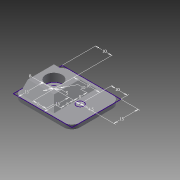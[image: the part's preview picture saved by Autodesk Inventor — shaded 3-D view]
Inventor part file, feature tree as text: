
AUTODESK INVENTOR PART (.ipt)
format: ipt  version: 2015 (Build 190159000, 159)  size: 124,416 bytes
history: native  units: mm
features: fillet x4, extrude x3, chamfer x3, sketch x1
ambient origin geometry x8: Origin, YZ Plane, XZ Plane, XY Plane, X Axis, Y Axis, Z Axis, Center Point
bodies: Solid1 (feature_tree)
feature tree (11):
  sketch  "Sketch1"  dims[d0=10.0mm d1=16.0mm d2=4.5mm d3=5.0mm d4=15.0mm d5=15.0mm d6=10.0mm d7=15.0mm d9=2.5mm d10=0.0mm d13=5.0mm d14=0.0mm d15=10.0mm d16=8.0mm d17=8.0mm d18=8.0mm d19=8.0mm d20=5.0mm d21=0.0mm d22=5.0mm d23=2.0mm d24=45.0deg d25=5.0mm d26=2.0mm d27=45.0deg d31=5.0mm d32=2.0mm d33=45.0deg d34=5.0mm d35=5.0mm d36=5.0mm d37=5.0mm]
  extrude  "Extrusion1"  Depth=5.0mm
  extrude  "Extrusion3"  Depth=5.0mm
  extrude  "Extrusion4"  Depth=5.0mm
  chamfer  "Chamfer1"  Distance=15.0mm
  chamfer  "Chamfer2"  Distance=15.0mm
  chamfer  "Chamfer4"  Distance=10.0mm
  fillet  "Fillet1"  Radius=15.0mm
  fillet  "Fillet2"  Radius=2.5mm
  fillet  "Fillet3"  Radius=5.0mm
  fillet  "Fillet4"  Radius=10.0mm
